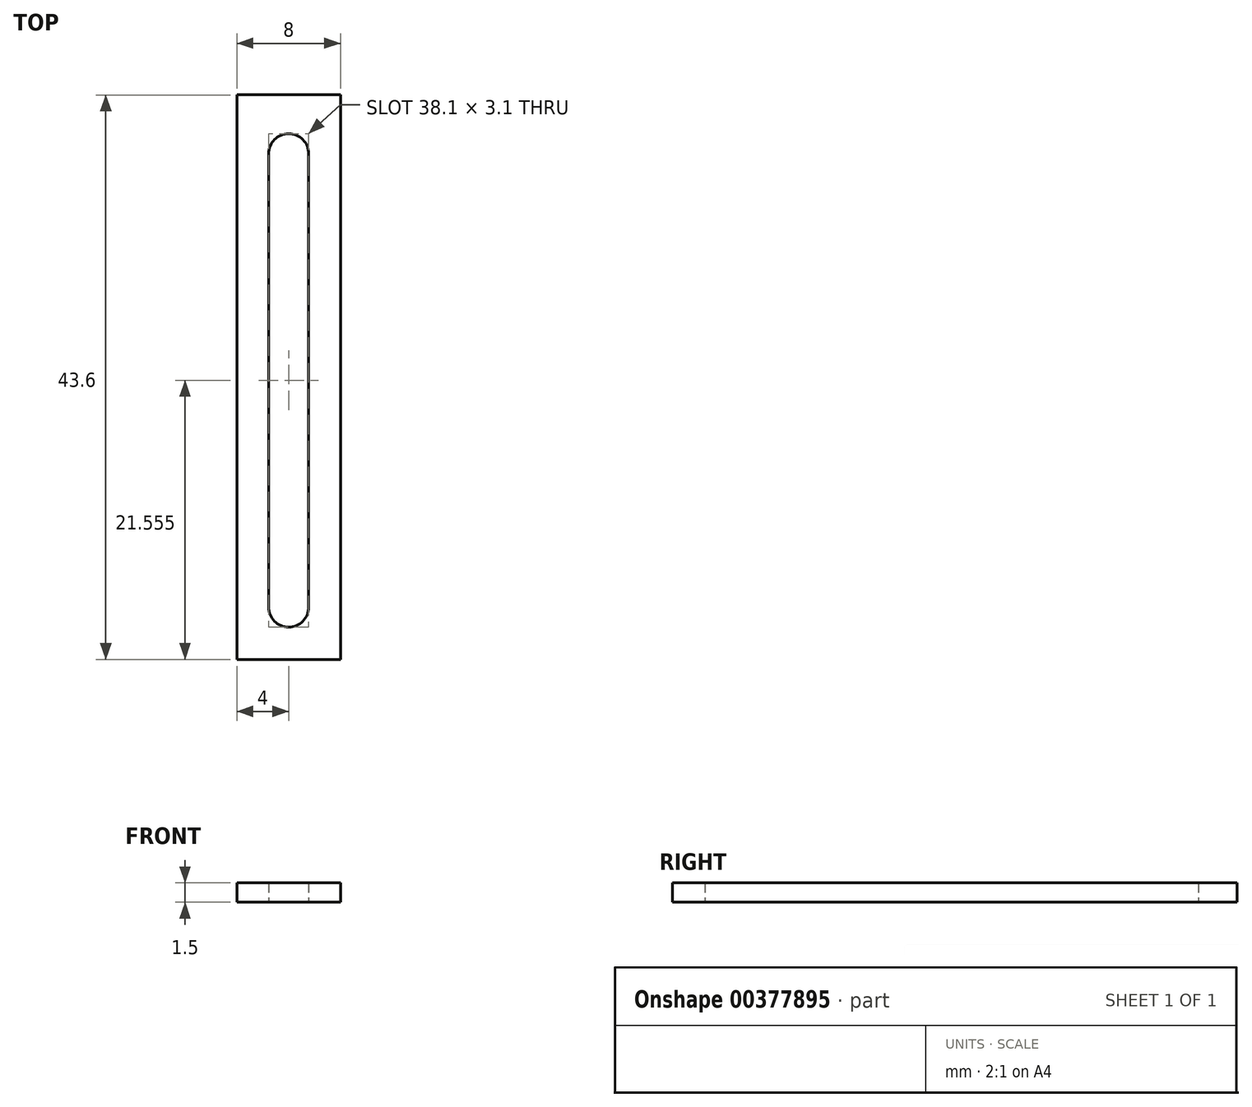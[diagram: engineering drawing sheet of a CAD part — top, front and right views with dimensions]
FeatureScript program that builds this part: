
annotation { "Feature Type Name" : "Feature", "Feature Type Description" : "" }
export const myFeature = defineFeature(function(context is Context, id is Id, definition is map)
    precondition{}
    {
        {
            var Q0;
            Q0=qCreatedBy(makeId("Top.planeOp"),FACE);
            var sketch = newSketch(context, id + "F0", { "sketchPlane" : qUnion([Q0])});
            skLineSegment(sketch, "E0.bottom", {"start": v(-13, 39.02) * mm, "end": v(13, 39.02) * mm});
            skLineSegment(sketch, "E0.top", {"start": v(-13, -39.02) * mm, "end": v(13, -39.02) * mm});
            skLineSegment(sketch, "E0.left", {"start": v(-13, 39.02) * mm, "end": v(-13, -39.02) * mm});
            skLineSegment(sketch, "E0.right", {"start": v(13, 39.02) * mm, "end": v(13, -39.02) * mm});
            skPoint(sketch, "E0.middle", {"position": v(0, 0) * mm});
            skCircle(sketch, "E1", {"center": v(-10.5, -36.52) * mm, "radius": 1 * mm});
            skCircle(sketch, "E2", {"center": v(-10.5, -15.53) * mm, "radius": 1 * mm});
            skCircle(sketch, "E3", {"center": v(0, -15.53) * mm, "radius": 6.25 * mm});
            skArc(sketch, "E4", {"start": v(-5.73, -39.02) * mm, "mid": v(0, -42.77) * mm, "end": v(5.73, -39.02) * mm, "construction": true});
            skCircle(sketch, "E5.MirrorC", {"center": v(10.5, -15.53) * mm, "radius": 1 * mm});
            skCircle(sketch, "E6.MirrorC", {"center": v(10.5, -36.52) * mm, "radius": 1 * mm});
            skLineSegment(sketch, "E7.bottom", {"start": v(-1.55, 34.48) * mm, "end": v(1.55, 34.48) * mm});
            skLineSegment(sketch, "E7.top", {"start": v(-1.55, -0.53) * mm, "end": v(1.55, -0.53) * mm});
            skLineSegment(sketch, "E7.left", {"start": v(-1.55, 34.48) * mm, "end": v(-1.55, -0.53) * mm});
            skLineSegment(sketch, "E7.right", {"start": v(1.55, 34.48) * mm, "end": v(1.55, -0.53) * mm});
            skPoint(sketch, "E7.middle", {"position": v(0, 16.97) * mm});
            skArc(sketch, "E8", {"start": v(1.55, 34.48) * mm, "mid": v(0, 36.02) * mm, "end": v(-1.55, 34.48) * mm});
            skLineSegment(sketch, "E9", {"start": v(-1.55, 16.97) * mm, "end": v(1.55, 16.97) * mm, "construction": true});
            skArc(sketch, "E10.MirrorCS", {"start": v(1.55, -0.53) * mm, "mid": v(0, -2.08) * mm, "end": v(-1.55, -0.53) * mm});
            skLineSegment(sketch, "E11", {"start": v(-6.25, -36.53) * mm, "end": v(-6.25, -39.03) * mm});
            skLineSegment(sketch, "E12.MirrorCS", {"start": v(6.25, -36.53) * mm, "end": v(6.25, -39.03) * mm});
            skArc(sketch, "E13.trimOffspring", {"start": v(6.25, -36.53) * mm, "mid": v(0, -30.28) * mm, "end": v(-6.25, -36.53) * mm});
            skLineSegment(sketch, "E14", {"start": v(-10.5, -15.53) * mm, "end": v(-10.5, -36.52) * mm, "construction": true});
            skCircle(sketch, "E15", {"center": v(0, -26.02) * mm, "radius": 2 * mm});
            skPoint(sketch, "E15.centerSnap0", {"position": v(-10.5, -26.03) * mm});
            skSolve(sketch);
        }
        {
            var Q0;
            Q0=makeQuery(id+"F0.imprint","IMPRINT",FACE,{"disambiguationData":[TD([[makeQuery(id+"F0.imprint","IMPRINT",EDGE,{"derivedFrom":sQuery(id+"F0.wireOp",EDGE,"E0.bottom")}),-1.0]])]});
            extrude(context, id + "F1", {"entities" : qUnion([Q0]), "depth" : 1.5 * mm});
        }
        {
            var Q0;
            Q0=makeQuery(id+"F1.opExtrude","CAP_FACE",FACE,{"disambiguationData":[OSD([sQuery(id+"F0.wireOp",EDGE,"E0.bottom"),sQuery(id+"F0.wireOp",EDGE,"E0.top"),sQuery(id+"F0.wireOp",EDGE,"E0.left"),sQuery(id+"F0.wireOp",EDGE,"E0.right"),sQuery(id+"F0.wireOp",EDGE,"E1"),sQuery(id+"F0.wireOp",EDGE,"E2"),sQuery(id+"F0.wireOp",EDGE,"E3"),sQuery(id+"F0.wireOp",EDGE,"E5.MirrorC"),sQuery(id+"F0.wireOp",EDGE,"E6.MirrorC"),sQuery(id+"F0.wireOp",EDGE,"E7.left"),sQuery(id+"F0.wireOp",EDGE,"E7.right"),sQuery(id+"F0.wireOp",EDGE,"E8"),sQuery(id+"F0.wireOp",EDGE,"E10.MirrorCS"),sQuery(id+"F0.wireOp",EDGE,"E11"),sQuery(id+"F0.wireOp",EDGE,"E12.MirrorCS"),sQuery(id+"F0.wireOp",EDGE,"E13.trimOffspring"),sQuery(id+"F0.wireOp",EDGE,"E15")])],"isStart":false});
            var sketch = newSketch(context, id + "F2", { "sketchPlane" : qUnion([Q0])});
            skLineSegment(sketch, "E16.bottom", {"start": v(-13, -39.02) * mm, "end": v(13, -39.02) * mm});
            skLineSegment(sketch, "E16.top", {"start": v(-13, -4.58) * mm, "end": v(13, -4.58) * mm});
            skLineSegment(sketch, "E16.left", {"start": v(-13, -39.02) * mm, "end": v(-13, -4.58) * mm});
            skLineSegment(sketch, "E16.right", {"start": v(13, -39.02) * mm, "end": v(13, -4.58) * mm});
            skLineSegment(sketch, "E17.bottom", {"start": v(-13, 39.02) * mm, "end": v(-4, 39.02) * mm});
            skLineSegment(sketch, "E17.top", {"start": v(-13, -4.58) * mm, "end": v(-4, -4.58) * mm});
            skLineSegment(sketch, "E17.left", {"start": v(-13, 39.02) * mm, "end": v(-13, -4.58) * mm});
            skLineSegment(sketch, "E17.right", {"start": v(-4, 39.02) * mm, "end": v(-4, -4.58) * mm});
            skLineSegment(sketch, "E18.MirrorCS", {"start": v(13, 39.02) * mm, "end": v(4, 39.02) * mm});
            skLineSegment(sketch, "E19.MirrorCS", {"start": v(4, 39.02) * mm, "end": v(4, -4.58) * mm});
            skLineSegment(sketch, "E20.MirrorCS", {"start": v(13, 39.02) * mm, "end": v(13, -4.58) * mm});
            skSolve(sketch);
        }
        {
            var Q0;
            Q0=makeQuery(id+"F2.imprint","IMPRINT",FACE,{"disambiguationData":[TD([[makeQuery(id+"F2.imprint","IMPRINT",EDGE,{"derivedFrom":sQuery(id+"F2.wireOp",EDGE,"E16.top")}),-1.0]])]});
            var Q1;
            Q1=makeQuery(id+"F2.imprint","IMPRINT",FACE,{"disambiguationData":[TD([[makeQuery(id+"F2.imprint","IMPRINT",EDGE,{"derivedFrom":sQuery(id+"F2.wireOp",EDGE,"E17.bottom")}),-1.0]])]});
            var Q2;
            Q2=makeQuery(id+"F2.imprint","IMPRINT",FACE,{"disambiguationData":[TD([[makeQuery(id+"F2.imprint","IMPRINT",EDGE,{"derivedFrom":sQuery(id+"F2.wireOp",EDGE,"E18.MirrorCS")}),-1.0]])]});
            extrude(context, id + "F3", {"entities" : qUnion([Q0, Q1, Q2]), "operationType" : NewBodyOperationType.REMOVE, "endBound" : BoundingType.UP_TO_NEXT, "oppositeDirection" : true, "depth" : 25 * mm});
        }
    });
